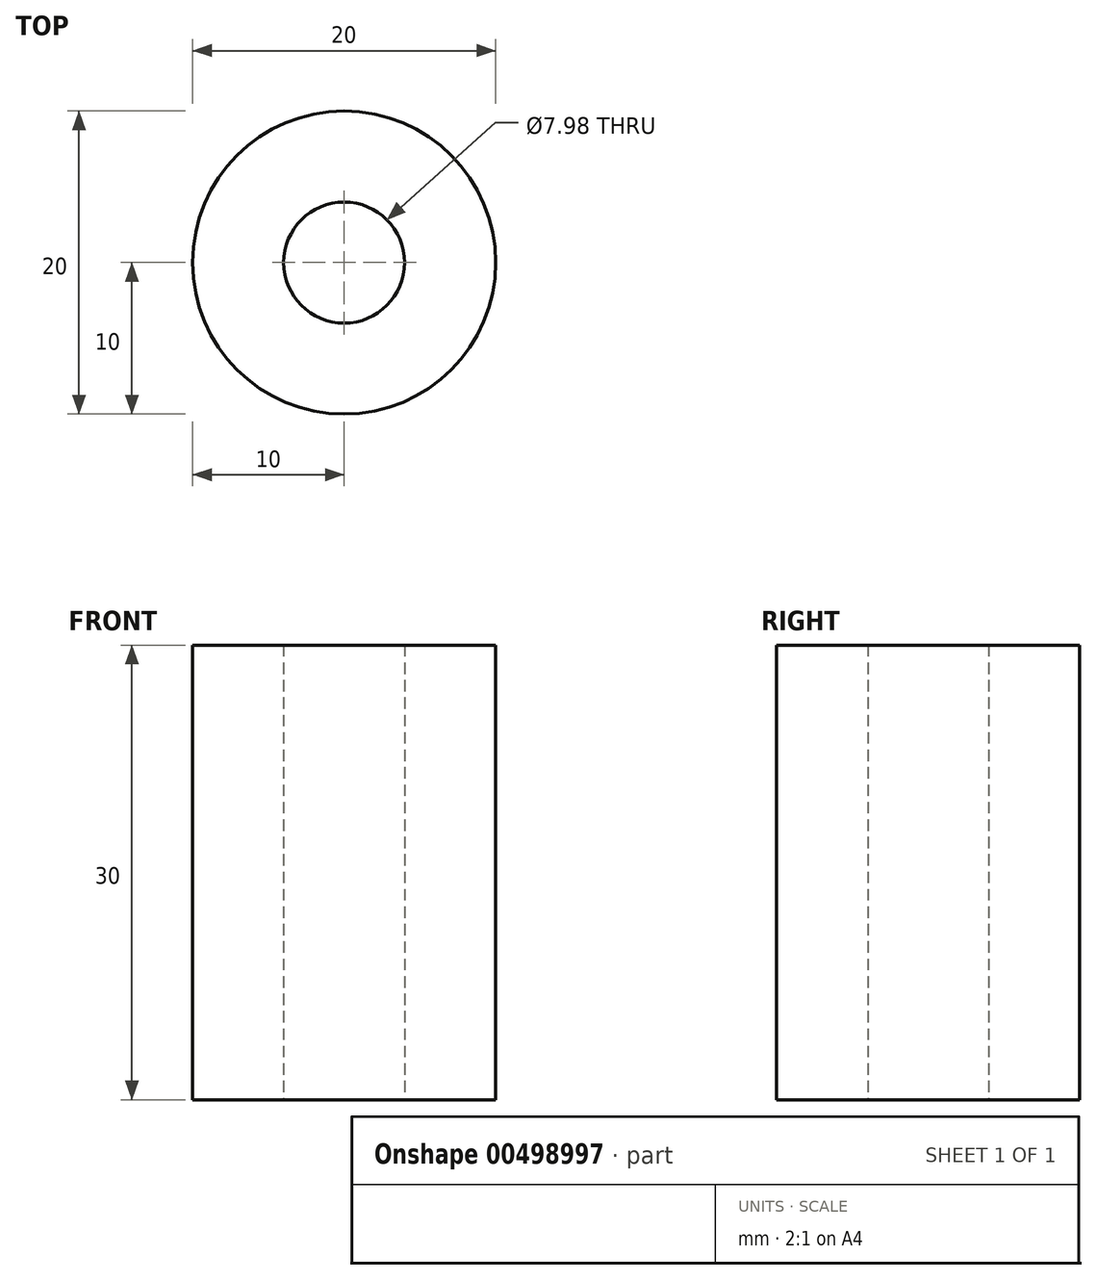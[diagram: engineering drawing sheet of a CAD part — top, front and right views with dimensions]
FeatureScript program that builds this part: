
annotation { "Feature Type Name" : "Feature", "Feature Type Description" : "" }
export const myFeature = defineFeature(function(context is Context, id is Id, definition is map)
    precondition{}
    {
        {
            var Q0;
            Q0=qCreatedBy(makeId("Top.planeOp"),FACE);
            var sketch = newSketch(context, id + "F0", { "sketchPlane" : qUnion([Q0])});
            skCircle(sketch, "E0", {"center": v(0, 0) * mm, "radius": 10 * mm});
            skCircle(sketch, "E1", {"center": v(0, 0) * mm, "radius": 4 * mm});
            skSolve(sketch);
        }
        {
            var Q0;
            Q0 = qSketchRegion(id + "F0", true);
            extrude(context, id + "F1", {"entities" : qUnion([Q0]), "depth" : 30 * mm});
        }
    });
